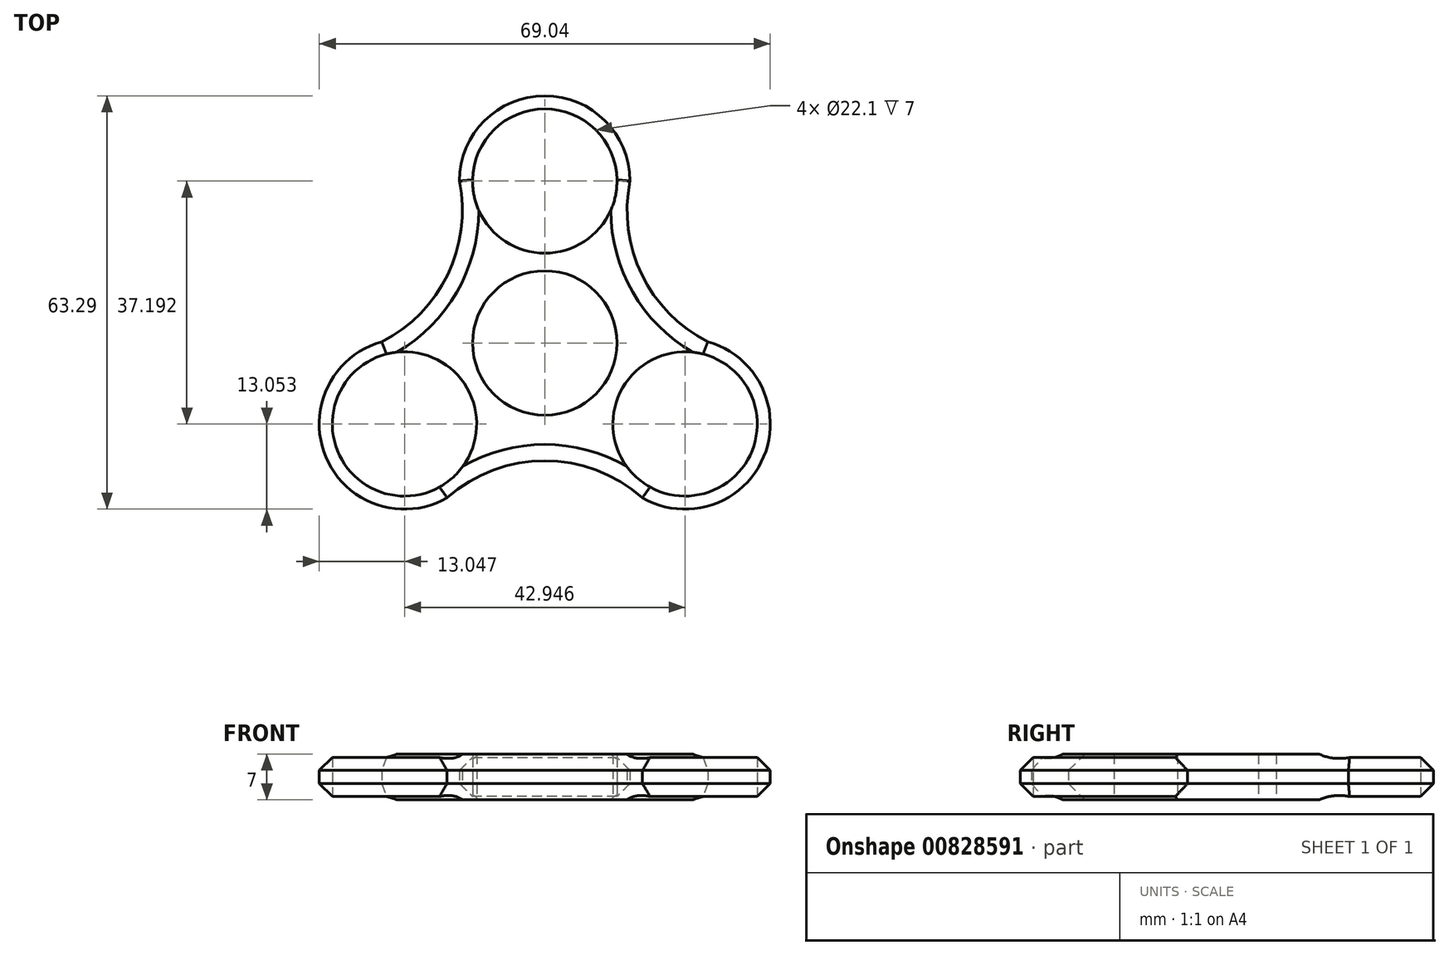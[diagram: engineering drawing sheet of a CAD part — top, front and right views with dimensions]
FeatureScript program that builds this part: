
annotation { "Feature Type Name" : "Feature", "Feature Type Description" : "" }
export const myFeature = defineFeature(function(context is Context, id is Id, definition is map)
    precondition{}
    {
        {
            var Q0;
            Q0=qCreatedBy(makeId("Top.planeOp"),FACE);
            var sketch = newSketch(context, id + "F0", { "sketchPlane" : qUnion([Q0])});
            skCircle(sketch, "E0", {"center": v(0, 0) * mm, "radius": 11.05 * mm});
            skCircle(sketch, "E1", {"center": v(0, 24.8) * mm, "radius": 11.05 * mm});
            skArc(sketch, "E2", {"start": v(13.05, 24.8) * mm, "mid": v(0, 37.84) * mm, "end": v(-13.05, 24.8) * mm});
            skArc(sketch, "E3.1.0", {"start": v(-24.96, 0.18) * mm, "mid": v(-33.5, -17.44) * mm, "end": v(-14.95, -23.7) * mm});
            skCircle(sketch, "E3.1.1", {"center": v(-21.47, -12.4) * mm, "radius": 11.05 * mm});
            skArc(sketch, "E3.2.0", {"start": v(14.95, -23.7) * mm, "mid": v(33.5, -17.44) * mm, "end": v(24.96, 0.18) * mm});
            skCircle(sketch, "E3.2.1", {"center": v(21.47, -12.4) * mm, "radius": 11.05 * mm});
            skPoint(sketch, "E4.trimOffspring.end.orphan", {"position": v(13.05, 24.8) * mm});
            skPoint(sketch, "E5.1.0", {"position": v(-28, -1.1) * mm});
            skPoint(sketch, "E5.2.0", {"position": v(14.95, -23.7) * mm});
            skArc(sketch, "E6", {"start": v(-24.96, 0.18) * mm, "mid": v(-14.86, 10.48) * mm, "end": v(-13.05, 24.8) * mm});
            skArc(sketch, "E7.1.0", {"start": v(14.95, -23.7) * mm, "mid": v(0, -18.04) * mm, "end": v(-14.95, -23.7) * mm});
            skArc(sketch, "E7.2.0", {"start": v(13.05, 24.8) * mm, "mid": v(14.86, 10.48) * mm, "end": v(24.96, 0.18) * mm});
            skPoint(sketch, "E8.orphan", {"position": v(-14.95, -23.7) * mm});
            skPoint(sketch, "E9.orphan", {"position": v(28, -1.1) * mm});
            skPoint(sketch, "E10.orphan", {"position": v(-3.9, 24.8) * mm});
            skSolve(sketch);
        }
        {
            var Q0;
            Q0 = qSketchRegion(id + "F0", true);
            extrude(context, id + "F1", {"entities" : qUnion([Q0]), "depth" : 7 * mm, "offsetDistance" : 25 * mm});
        }
        {
            var Q0;
            Q0=makeQuery(id+"F1.opExtrude","CAP_EDGE",EDGE,{"disambiguationData":[OSD([sQuery(id+"F0.wireOp",EDGE,"E3.1.0")])],"isStart":false});
            var Q1;
            Q1=makeQuery(id+"F1.opExtrude","CAP_EDGE",EDGE,{"disambiguationData":[OSD([sQuery(id+"F0.wireOp",EDGE,"E7.1.0")])],"isStart":false});
            var Q2;
            Q2=makeQuery(id+"F1.opExtrude","CAP_EDGE",EDGE,{"disambiguationData":[OSD([sQuery(id+"F0.wireOp",EDGE,"E6")])],"isStart":false});
            var Q3;
            Q3=makeQuery(id+"F1.opExtrude","CAP_EDGE",EDGE,{"disambiguationData":[OSD([sQuery(id+"F0.wireOp",EDGE,"E3.2.0")])],"isStart":false});
            var Q4;
            Q4=makeQuery(id+"F1.opExtrude","CAP_EDGE",EDGE,{"disambiguationData":[OSD([sQuery(id+"F0.wireOp",EDGE,"E7.2.0")])],"isStart":false});
            var Q5;
            Q5=makeQuery(id+"F1.opExtrude","CAP_EDGE",EDGE,{"disambiguationData":[OSD([sQuery(id+"F0.wireOp",EDGE,"E2")])],"isStart":false});
            var Q6;
            Q6=makeQuery(id+"F1.opExtrude","CAP_EDGE",EDGE,{"disambiguationData":[OSD([sQuery(id+"F0.wireOp",EDGE,"E7.2.0")])],"isStart":true});
            var Q7;
            Q7=makeQuery(id+"F1.opExtrude","CAP_EDGE",EDGE,{"disambiguationData":[OSD([sQuery(id+"F0.wireOp",EDGE,"E2")])],"isStart":true});
            var Q8;
            Q8=makeQuery(id+"F1.opExtrude","CAP_EDGE",EDGE,{"disambiguationData":[OSD([sQuery(id+"F0.wireOp",EDGE,"E3.2.0")])],"isStart":true});
            var Q9;
            Q9=makeQuery(id+"F1.opExtrude","CAP_EDGE",EDGE,{"disambiguationData":[OSD([sQuery(id+"F0.wireOp",EDGE,"E7.1.0")])],"isStart":true});
            var Q10;
            Q10=makeQuery(id+"F1.opExtrude","CAP_EDGE",EDGE,{"disambiguationData":[OSD([sQuery(id+"F0.wireOp",EDGE,"E3.1.0")])],"isStart":true});
            var Q11;
            Q11=makeQuery(id+"F1.opExtrude","CAP_EDGE",EDGE,{"disambiguationData":[OSD([sQuery(id+"F0.wireOp",EDGE,"E6")])],"isStart":true});
            chamfer(context, id + "F2", {"entities" : qUnion([Q0, Q1, Q2, Q3, Q4, Q5, Q6, Q7, Q8, Q9, Q10, Q11]), "width" : 2.5 * mm, "tangentPropagation" : true});
        }
    });
